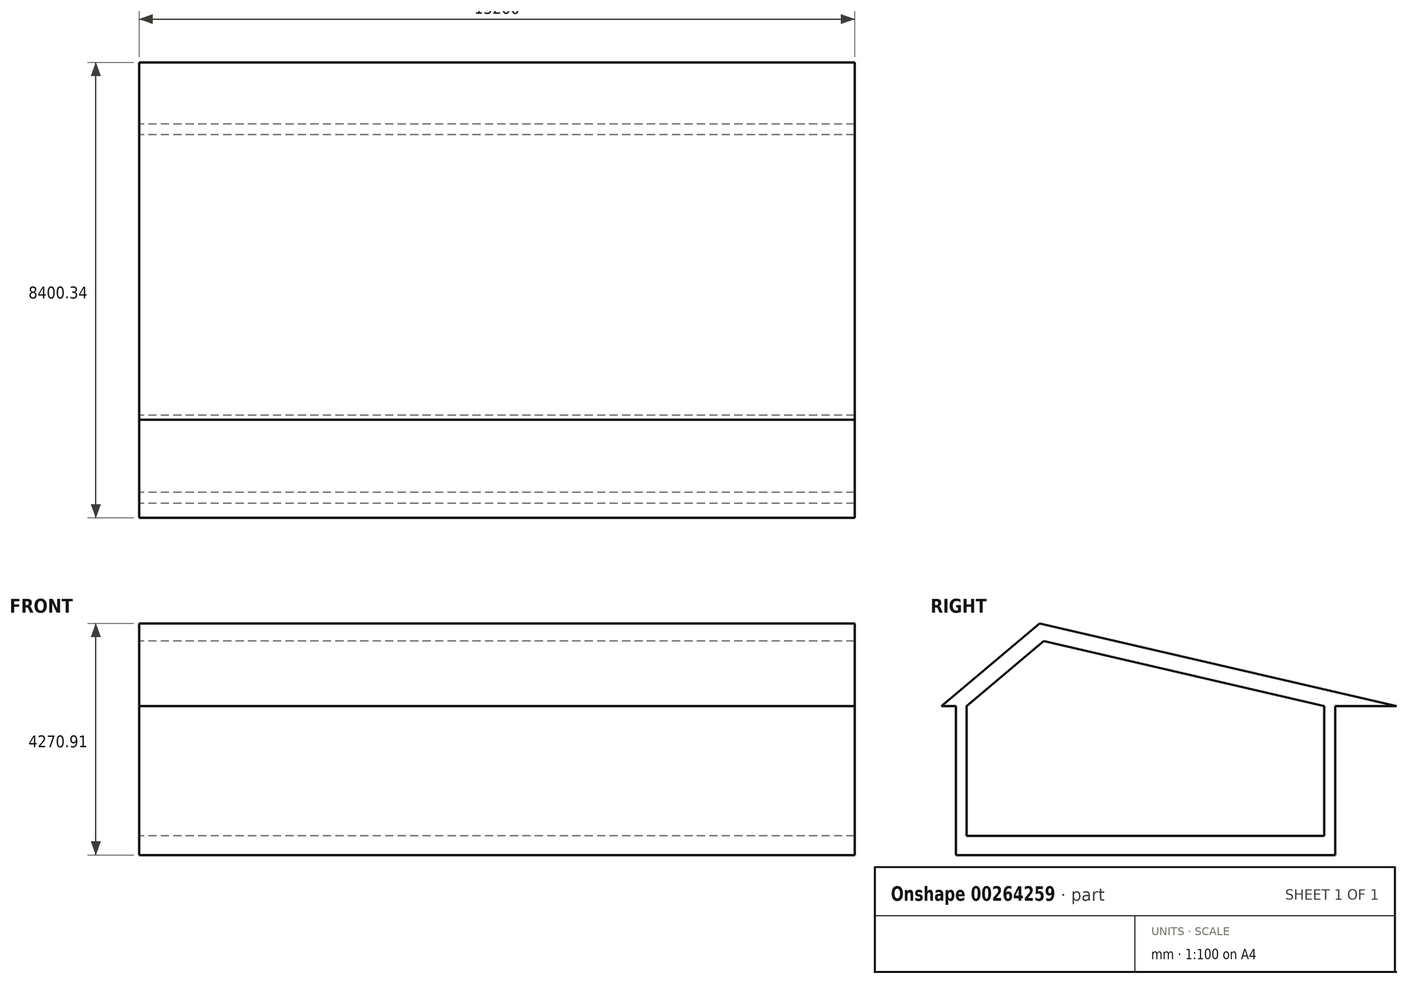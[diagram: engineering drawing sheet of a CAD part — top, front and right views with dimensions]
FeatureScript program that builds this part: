
annotation { "Feature Type Name" : "Feature", "Feature Type Description" : "" }
export const myFeature = defineFeature(function(context is Context, id is Id, definition is map)
    precondition{}
    {
        {
            var Q0;
            Q0=qCreatedBy(makeId("Right.planeOp"),FACE);
            var sketch = newSketch(context, id + "F0", { "sketchPlane" : qUnion([Q0])});
            skLineSegment(sketch, "E0", {"start": v(0, 0) * mm, "end": v(-6600, 0) * mm});
            skLineSegment(sketch, "E1", {"start": v(-6600, 0) * mm, "end": v(-6600, 2400) * mm});
            skLineSegment(sketch, "E2", {"start": v(-6600, 2400) * mm, "end": v(-5175.91, 3594.95) * mm});
            skLineSegment(sketch, "E3", {"start": v(-5175.91, 3594.95) * mm, "end": v(0, 2400) * mm});
            skLineSegment(sketch, "E4", {"start": v(0, 2400) * mm, "end": v(0, 0) * mm});
            skLineSegment(sketch, "E5", {"start": v(200, -350) * mm, "end": v(-6800, -350) * mm});
            skLineSegment(sketch, "E6", {"start": v(-6800, -350) * mm, "end": v(-6800, 2623.8) * mm});
            skLineSegment(sketch, "E7", {"start": v(-6800, 2623.8) * mm, "end": v(-5254.17, 3920.91) * mm});
            skLineSegment(sketch, "E8", {"start": v(-5254.17, 3920.91) * mm, "end": v(200, 2661.72) * mm});
            skLineSegment(sketch, "E9", {"start": v(200, 2661.72) * mm, "end": v(200, -350) * mm});
            skLineSegment(sketch, "E10", {"start": v(-6800, 2623.8) * mm, "end": v(-7066.72, 2400) * mm});
            skLineSegment(sketch, "E11", {"start": v(-7066.72, 2400) * mm, "end": v(-6800, 2400) * mm});
            skLineSegment(sketch, "E12", {"start": v(200, 2661.72) * mm, "end": v(1333.62, 2400) * mm});
            skLineSegment(sketch, "E13", {"start": v(1333.62, 2400) * mm, "end": v(0, 2400) * mm});
            skSolve(sketch);
        }
        {
            var Q0;
            Q0 = qSketchRegion(id + "F0", true);
            extrude(context, id + "F1", {"entities" : qUnion([Q0]), "depth" : 13200 * mm, "offsetDistance" : 25 * mm});
        }
    });
